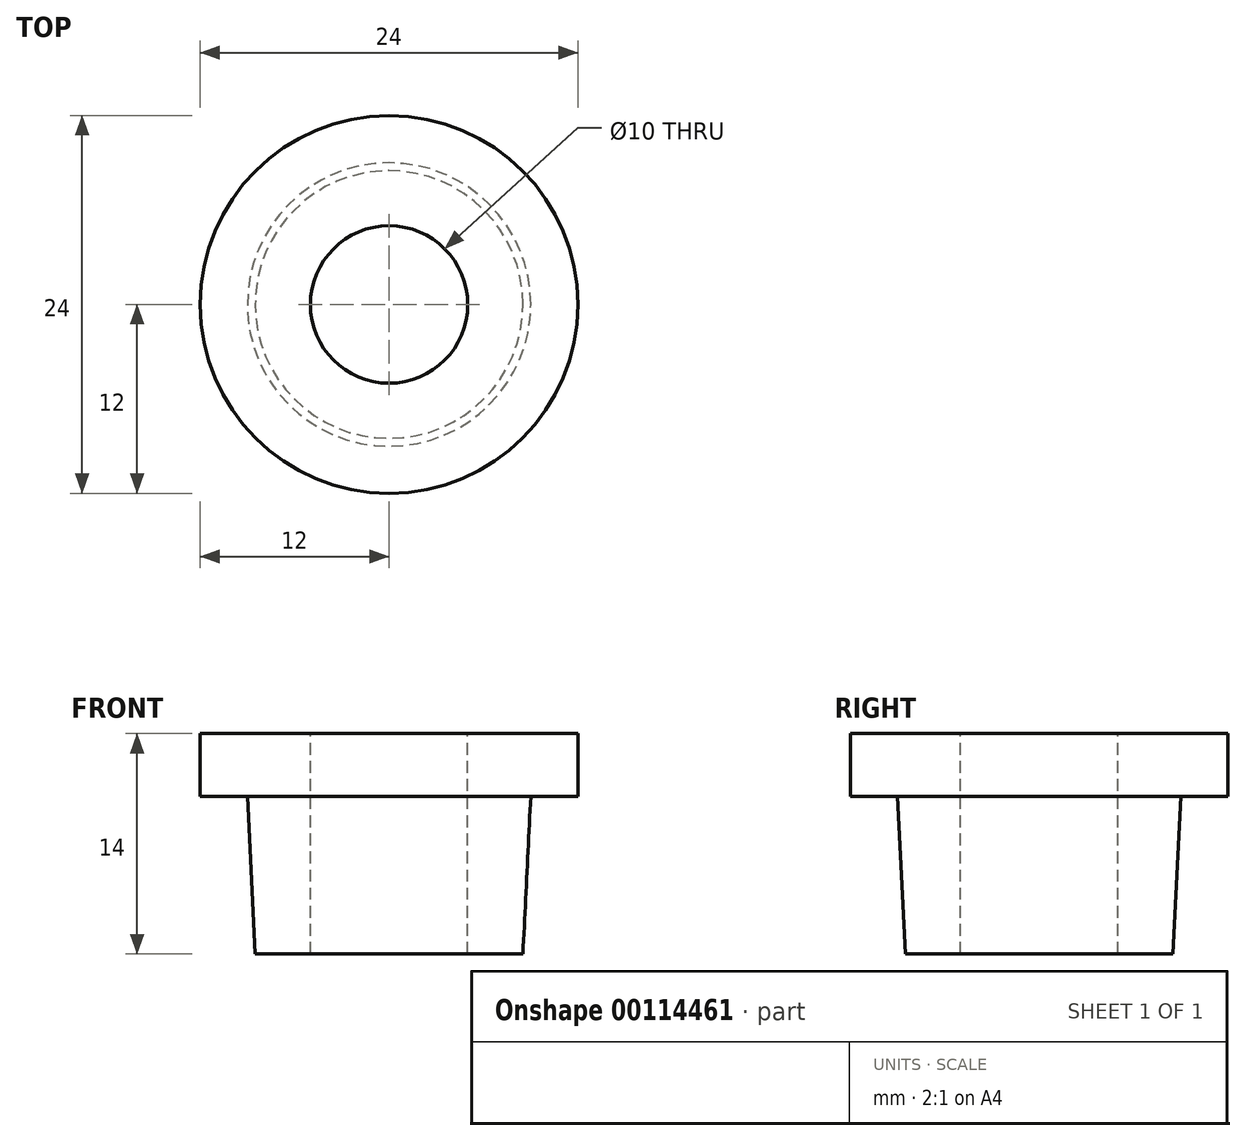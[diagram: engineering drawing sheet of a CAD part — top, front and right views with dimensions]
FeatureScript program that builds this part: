
annotation { "Feature Type Name" : "Feature", "Feature Type Description" : "" }
export const myFeature = defineFeature(function(context is Context, id is Id, definition is map)
    precondition{}
    {
        {
            var Q0;
            Q0=qCreatedBy(makeId("Right.planeOp"),FACE);
            var sketch = newSketch(context, id + "F0", { "sketchPlane" : qUnion([Q0])});
            skLineSegment(sketch, "E0", {"start": v(5, -14.59) * mm, "end": v(5, -0.59) * mm});
            skLineSegment(sketch, "E1", {"start": v(5, -0.59) * mm, "end": v(12, -0.59) * mm});
            skLineSegment(sketch, "E2", {"start": v(12, -0.59) * mm, "end": v(12, -4.59) * mm});
            skLineSegment(sketch, "E3", {"start": v(12, -4.59) * mm, "end": v(9, -4.59) * mm});
            skLineSegment(sketch, "E4", {"start": v(9, -4.59) * mm, "end": v(8.5, -14.59) * mm});
            skLineSegment(sketch, "E5", {"start": v(8.5, -14.59) * mm, "end": v(5, -14.59) * mm});
            skLineSegment(sketch, "E6", {"start": v(0, 8.4) * mm, "end": v(0, -25.78) * mm});
            skSolve(sketch);
        }
        {
            var Q0;
            {var subQ0=sQuery(id+"F0.wireOp",EDGE,"E0");Q0=makeQuery(id+"F0.imprint","IMPRINT",FACE,{"disambiguationData":[TD([[makeQuery(id+"F0.imprint","IMPRINT",EDGE,{"derivedFrom":subQ0}),-1.0]])]});}
            var Q1;
            Q1=sQuery(id+"F0.wireOp",EDGE,"E6");
            revolve(context, id + "F1", {"entities" : qUnion([Q0]), "axis" : qUnion([Q1]), "revolveType" : RevolveType.FULL});
        }
    });
